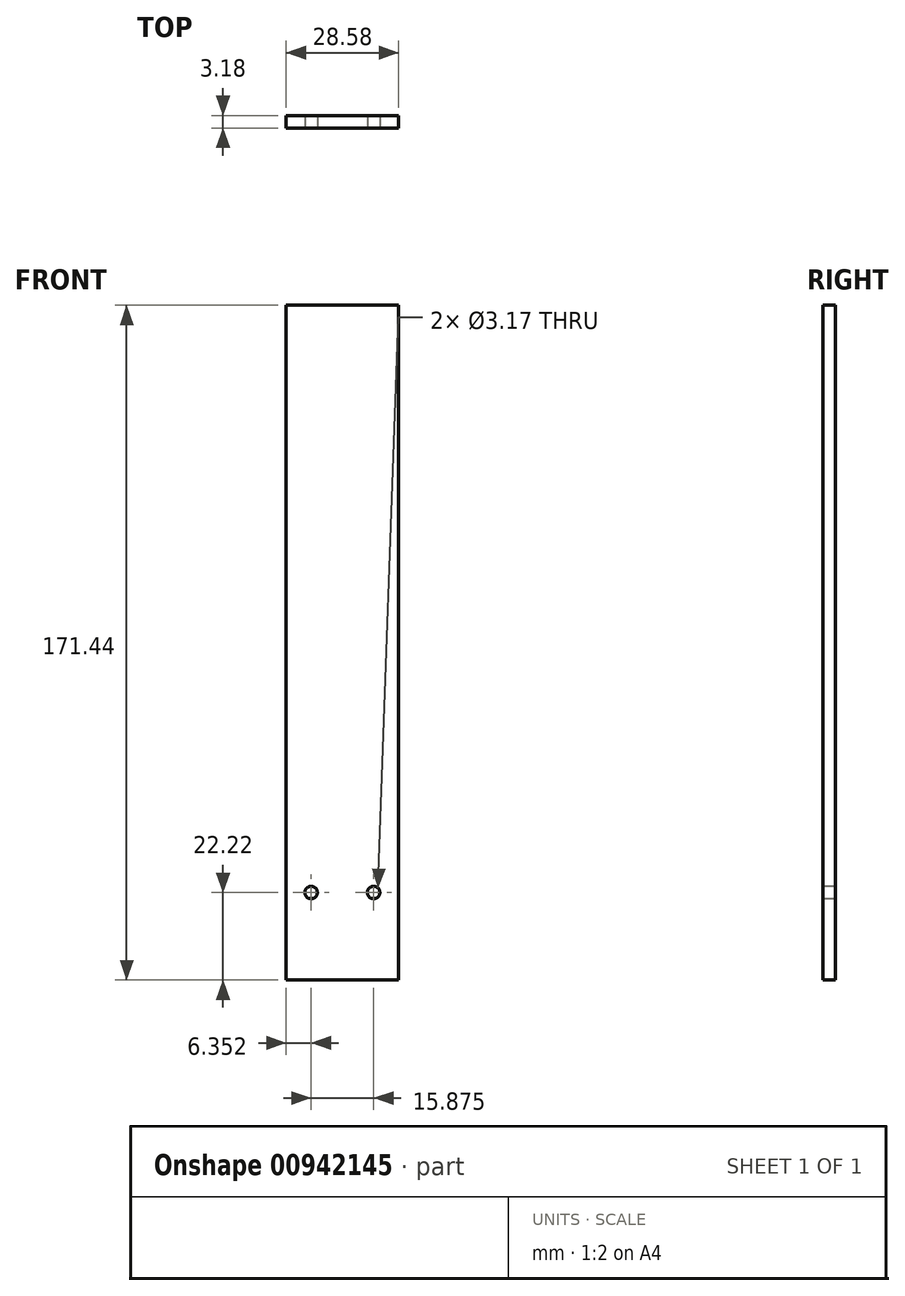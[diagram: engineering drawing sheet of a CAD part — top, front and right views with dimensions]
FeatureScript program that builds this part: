
annotation { "Feature Type Name" : "Feature", "Feature Type Description" : "" }
export const myFeature = defineFeature(function(context is Context, id is Id, definition is map)
    precondition{}
    {
        {
            var Q0;
            Q0=qCreatedBy(makeId("Front.planeOp"),FACE);
            var sketch = newSketch(context, id + "F0", { "sketchPlane" : qUnion([Q0])});
            skLineSegment(sketch, "E0.bottom", {"start": v(14.29, 85.73) * mm, "end": v(-14.29, 85.73) * mm});
            skLineSegment(sketch, "E0.top", {"start": v(14.29, -85.73) * mm, "end": v(-14.29, -85.73) * mm});
            skLineSegment(sketch, "E0.left", {"start": v(14.29, 85.72) * mm, "end": v(14.29, -85.73) * mm});
            skLineSegment(sketch, "E0.right", {"start": v(-14.29, 85.72) * mm, "end": v(-14.29, -85.73) * mm});
            skPoint(sketch, "E0.middle", {"position": v(0, 0) * mm});
            skCircle(sketch, "E1", {"center": v(7.94, -63.5) * mm, "radius": 1.59 * mm});
            skCircle(sketch, "E2", {"center": v(-7.94, -63.5) * mm, "radius": 1.59 * mm});
            skSolve(sketch);
        }
        {
            var Q0;
            Q0 = qSketchRegion(id + "F0", true);
            extrude(context, id + "F1", {"entities" : qUnion([Q0]), "endBound" : BoundingType.SYMMETRIC, "oppositeDirection" : true, "depth" : 3.17 * mm, "offsetDistance" : 25 * mm});
        }
    });
